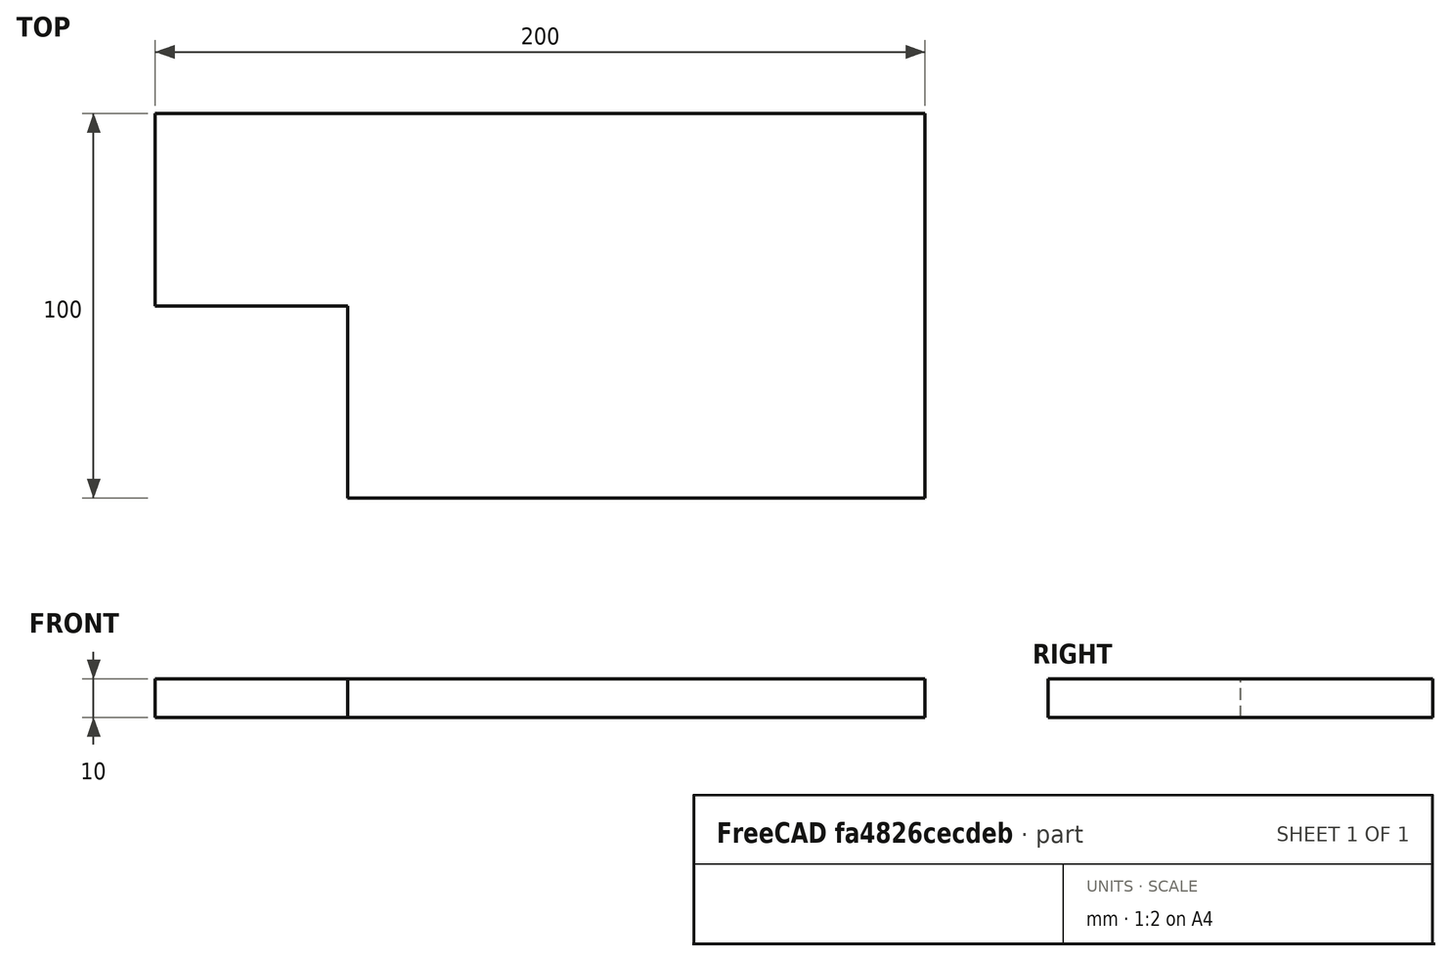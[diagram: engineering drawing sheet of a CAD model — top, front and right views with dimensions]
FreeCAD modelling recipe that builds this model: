
FCSTD DOCUMENT  (FreeCAD 0.21R33694 (Git))
Label: Plate_with_square_hole_Example
License: All rights reserved
LicenseURL: http://en.wikipedia.org/wiki/All_rights_reserved
objects: Fem::ConstraintDisplacement×3, Part::Box×2, App::MaterialObjectPython×1, Fem::FemSolverObjectPython×1, Part::Cut×1, Fem::ConstraintPressure×1, Fem::FemMeshObjectPython×1, Fem::FemAnalysis×1
note: 3 computed .brp shape members not serialized (recipe doc carries the construction recipe); baked Part::Feature solids carry a one-line shape summary decoded from their .brp

FEATURE [Part::Box] Box  label="Cube"
  AttacherType = Attacher::AttachEngine3D
  Height = 10
  Length = 200
  Width = 100
FEATURE [App::MaterialObjectPython] SolidMaterial  label="hdhdhd"  # material (typed FeaturePython)
  Category = 0
  Material = Density=7900.0 kg/m^3,Description=Standard steel material for CalculiX sample calculations,Father=Metal,Name=CalculiX-Steel,PoissonRatio=0.3,+4 more (map truncated)
FEATURE [Fem::FemSolverObjectPython] SolverCcxTools  # FEM object (typed FeaturePython)
  AnalysisType = 0
  BeamShellResultOutput3D = false
  BucklingFactors = 1
  EigenmodeHighLimit = 1000000
  EigenmodeLowLimit = 0
  EigenmodesCount = 10
  GeometricalNonlinearity = 1
  IterationsControlParameterCutb = 0.25,0.5,0.75,0.85,,,1.5,
  IterationsControlParameterIter = 4,8,9,200,10,400,,200,,
  IterationsControlParameterTimeUse = false
  IterationsThermoMechMaximum = 200
  IterationsUserDefinedIncrementations = false
  IterationsUserDefinedTimeStepLength = false
  MaterialNonlinearity = 1
  MatrixSolverType = 0
  SplitInputWriter = false
  ThermoMechSteadyState = true
  TimeEnd = 1
  TimeInitialStep = 1
FEATURE [Part::Box] Box001  label="Cube001"
  AttacherType = Attacher::AttachEngine3D
  Height = 10
  Length = 100
  Placement = pos=(-50,-50,0) rot=(0,0,1;0rad)
  Width = 100
FEATURE [Part::Cut] Cut
  Base = -> Box
  Tool = -> Box001
FEATURE [Fem::ConstraintDisplacement] FemConstraintDisplacement
  NormalDirection = (-1,0,0)
  Normals = (12) [(-1,0,0),(-1,0,0),(-1,0,0),(-1,0,0),(-1,0,0),(-1,0,0),(-1,0,0),(-1,0,0),(-1,0,0),(-1,0,0),(-1,0,0),(-1,0,0)]
  Points = (12) [(0,100,0),(0,100,5),(0,100,10),(0,83.3333,0),(0,83.3333,5),(0,83.3333,10),(0,66.6667,0),(0,66.6667,5),(0,66.6667,10),(0,50,0),(0,50,5),(0,50,10)]
  References = -> [Cut]
  hasXFormula = false
  hasYFormula = false
  hasZFormula = false
  rotxFix = false
  rotxFree = true
  rotyFix = false
  rotyFree = true
  rotzFix = false
  rotzFree = true
  useFlowSurfaceForce = false
  xDisplacement = 0
  xFix = true
  xFree = false
  xRotation = 0
  yDisplacement = 0
  yFix = false
  yFree = true
  yRotation = 0
  zDisplacement = 0
  zFix = false
  zFree = true
  zRotation = 0
FEATURE [Fem::ConstraintDisplacement] FemConstraintDisplacement001
  NormalDirection = (0,-1,0)
  Normals = (12) [(0,-1,0),(0,-1,0),(0,-1,0),(0,-1,0),(0,-1,0),(0,-1,0),(0,-1,0),(0,-1,0),(0,-1,0),(0,-1,0),(0,-1,0),(0,-1,0)]
  Points = (12) [(50,0,0),(50,0,5),(50,0,10),(100,0,0),(100,0,5),(100,0,10),(150,0,0),(150,0,5),(150,0,10),(200,0,0),(200,0,5),(200,0,10)]
  References = -> [Cut]
  hasXFormula = false
  hasYFormula = false
  hasZFormula = false
  rotxFix = false
  rotxFree = true
  rotyFix = false
  rotyFree = true
  rotzFix = false
  rotzFree = true
  useFlowSurfaceForce = false
  xDisplacement = 0
  xFix = false
  xFree = true
  xRotation = 0
  yDisplacement = 0
  yFix = true
  yFree = false
  yRotation = 0
  zDisplacement = 0
  zFix = false
  zFree = true
  zRotation = 0
FEATURE [Fem::ConstraintPressure] FemConstraintPressure
  NormalDirection = (1,0,0)
  Normals = (12) [(1,0,0),(1,0,0),(1,0,0),(1,0,0),(1,0,0),(1,0,0),(1,0,0),(1,0,0),(1,0,0),(1,0,0),(1,0,0),(1,0,0)]
  Points = (12) [(200,100,0),(200,100,5),(200,100,10),(200,66.6667,0),(200,66.6667,5),(200,66.6667,10),(200,33.3333,0),(200,33.3333,5),(200,33.3333,10),(200,0,0),+2 more]
  Pressure = 50
  References = -> [Cut]
  Reversed = true
FEATURE [Fem::ConstraintDisplacement] FemConstraintDisplacement002
  NormalDirection = (0,0,-1)
  Normals = (14) [(0,0,-1),(0,0,-1),(0,0,-1),(0,0,-1),(0,0,-1),(0,0,-1),(0,0,-1),(0,0,-1),(0,0,-1),(0,0,-1),(0,0,-1),(0,0,-1),(0,0,-1),(0,0,-1)]
  Points = (14) [(66.6667,0,0),(133.333,0,0),(200,0,0),(66.6667,33.3333,0),(133.333,33.3333,0),(200,33.3333,0),(0,66.6667,0),(66.6667,66.6667,0),(133.333,66.6667,0),+5 more]
  References = -> [Cut]
  Scale = 13
  hasXFormula = false
  hasYFormula = false
  hasZFormula = false
  rotxFix = false
  rotxFree = true
  rotyFix = false
  rotyFree = true
  rotzFix = false
  rotzFree = true
  useFlowSurfaceForce = false
  xDisplacement = 0
  xFix = false
  xFree = true
  xRotation = 0
  yDisplacement = 0
  yFix = false
  yFree = true
  yRotation = 0
  zDisplacement = 0
  zFix = true
  zFree = false
  zRotation = 0
FEATURE [Fem::FemMeshObjectPython] FEMMeshGmsh  # FEM object (typed FeaturePython)
  Algorithm2D = 0
  Algorithm3D = 0
  CharacteristicLengthMax = 0
  CharacteristicLengthMin = 0
  CoherenceMesh = true
  ElementDimension = 0
  ElementOrder = 1
  GeometryTolerance = 1e-06
  GroupsOfNodes = false
  HighOrderOptimize = 0
  MeshSizeFromCurvature = 12
  OptimizeNetgen = false
  OptimizeStd = true
  Part = -> Cut
  RecombinationAlgorithm = 0
  Recombine3DAll = false
  RecombineAll = false
  SecondOrderLinear = false
FEATURE [Fem::FemAnalysis] Analysis
  Group = -> [SolverCcxTools,FemConstraintDisplacement,FemConstraintDisplacement001,FemConstraintPressure,SolidMaterial,FemConstraintDisplacement002,FEMMeshGmsh]
